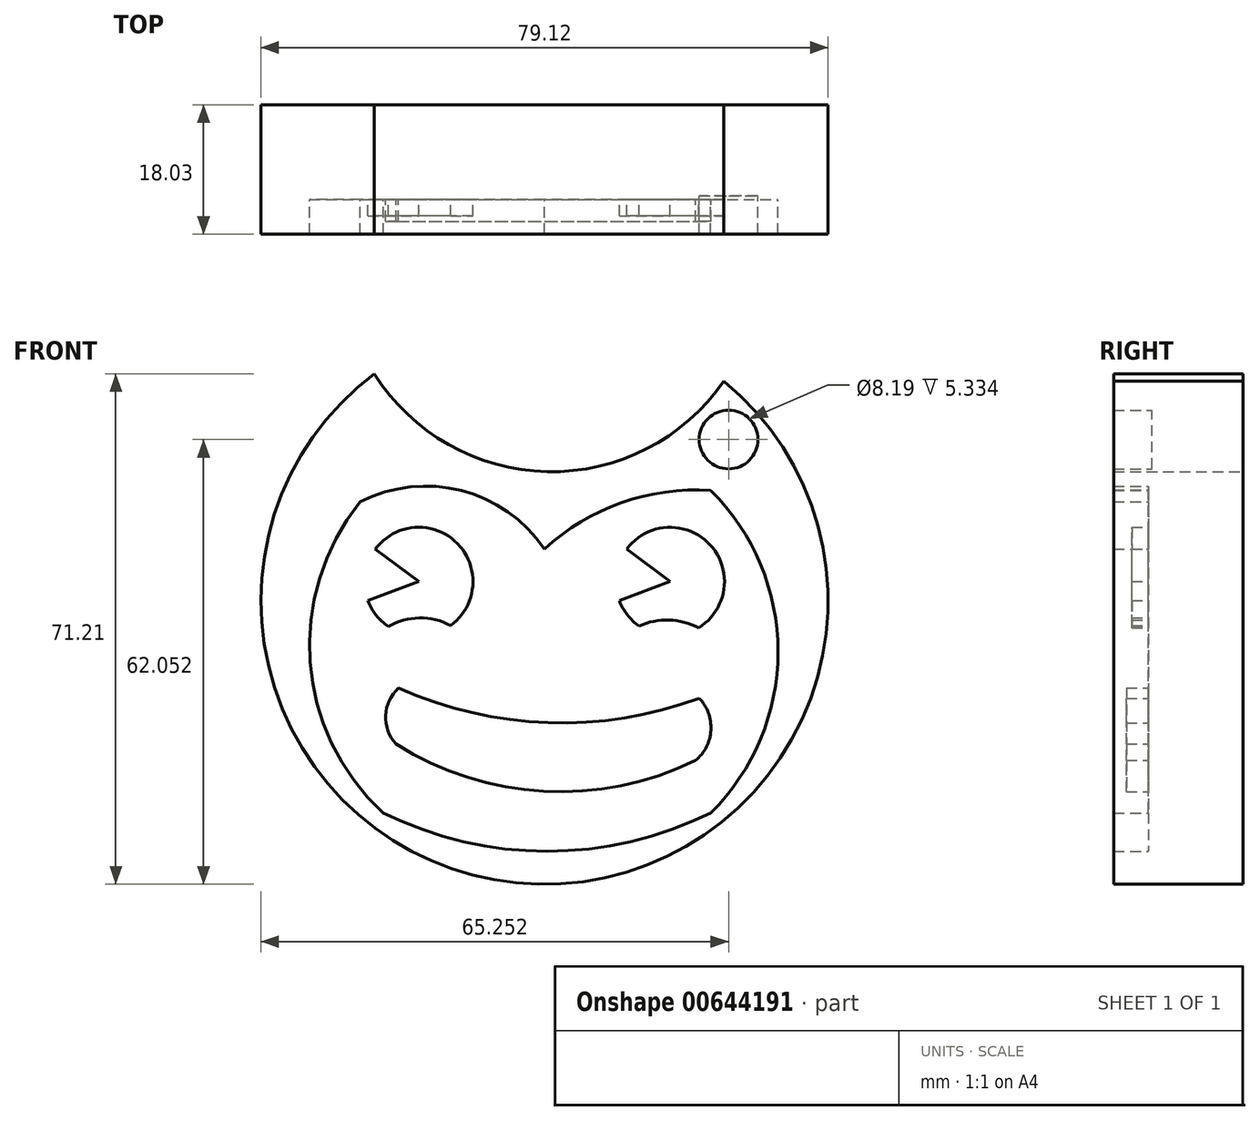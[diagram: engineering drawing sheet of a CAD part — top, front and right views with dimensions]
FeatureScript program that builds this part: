
annotation { "Feature Type Name" : "Feature", "Feature Type Description" : "" }
export const myFeature = defineFeature(function(context is Context, id is Id, definition is map)
    precondition{}
    {
        {
            var Q0;
            Q0=qCreatedBy(makeId("Front.planeOp"),FACE);
            var sketch = newSketch(context, id + "F0", { "sketchPlane" : qUnion([Q0])});
            skArc(sketch, "E0", {"start": v(-23.73, 31.65) * mm, "mid": v(-0.83, -39.55) * mm, "end": v(25.03, 30.64) * mm});
            skArc(sketch, "E1", {"start": v(-23.73, 31.65) * mm, "mid": v(0.38, 18) * mm, "end": v(25.03, 30.64) * mm});
            skSolve(sketch);
        }
        {
            var Q0;
            Q0=makeQuery(id+"F0.imprint","IMPRINT",FACE,{"disambiguationData":[TD([[makeQuery(id+"F0.imprint","IMPRINT",EDGE,{"derivedFrom":sQuery(id+"F0.wireOp",EDGE,"E0")}),1.0]])]});
            extrude(context, id + "F1", {"entities" : qUnion([Q0]), "depth" : 12.7 * mm, "offsetDistance" : 25.4 * mm});
        }
        {
            var Q0;
            Q0=makeQuery(id+"F1.opExtrude","CAP_FACE",FACE,{"disambiguationData":[OSD([sQuery(id+"F0.wireOp",EDGE,"E0"),sQuery(id+"F0.wireOp",EDGE,"E1")])],"isStart":false});
            var sketch = newSketch(context, id + "F2", { "sketchPlane" : qUnion([Q0])});
            skArc(sketch, "E2", {"start": v(-24.63, 0) * mm, "mid": v(-23.49, -2.01) * mm, "end": v(-21.8, -3.59) * mm});
            skArc(sketch, "E3.MirrorC", {"start": v(11.48, 7.2) * mm, "mid": v(23.13, 7.78) * mm, "end": v(21.5, -3.78) * mm});
            skLineSegment(sketch, "E4", {"start": v(-24.63, 0) * mm, "end": v(-17.54, 2.68) * mm});
            skLineSegment(sketch, "E5", {"start": v(-17.54, 2.68) * mm, "end": v(-23.61, 7.2) * mm});
            skLineSegment(sketch, "E6", {"start": v(10.46, 0) * mm, "end": v(17.54, 2.68) * mm});
            skLineSegment(sketch, "E7", {"start": v(17.54, 2.68) * mm, "end": v(11.48, 7.2) * mm});
            skArc(sketch, "E8", {"start": v(-10.05, -6.13) * mm, "mid": v(-17.34, -2.4) * mm, "end": v(-24.63, -6.13) * mm});
            skArc(sketch, "E9", {"start": v(25.16, -7.2) * mm, "mid": v(17.2, -2.69) * mm, "end": v(9.16, -7.02) * mm});
            skArc(sketch, "E10.trimOffspring", {"start": v(-13.1, -3.46) * mm, "mid": v(-12.15, 8) * mm, "end": v(-23.61, 7.2) * mm});
            skArc(sketch, "E11.trimOffspring", {"start": v(13.2, -3.53) * mm, "mid": v(11.57, -1.97) * mm, "end": v(10.46, 0) * mm});
            skSolve(sketch);
        }
        {
            var Q0;
            Q0=makeQuery(id+"F2.imprint","IMPRINT",FACE,{"disambiguationData":[TD([[makeQuery(id+"F2.imprint","IMPRINT",EDGE,{"derivedFrom":sQuery(id+"F2.wireOp",EDGE,"E2")}),-1.0]])]});
            var sketch = newSketch(context, id + "F3", { "sketchPlane" : qUnion([Q0])});
            skArc(sketch, "E12", {"start": v(-20.36, -12.18) * mm, "mid": v(0.48, -17.02) * mm, "end": v(21.6, -13.6) * mm});
            skArc(sketch, "E13", {"start": v(-20.71, -20) * mm, "mid": v(-0.11, -26.59) * mm, "end": v(21.09, -22.28) * mm});
            skArc(sketch, "E14", {"start": v(-20.36, -12.18) * mm, "mid": v(-22.16, -16.02) * mm, "end": v(-20.71, -20) * mm});
            skArc(sketch, "E15", {"start": v(21.09, -22.28) * mm, "mid": v(23.22, -18.05) * mm, "end": v(21.6, -13.6) * mm});
            skLineSegment(sketch, "E16", {"start": v(-17.1, -22.05) * mm, "end": v(-16.62, -13.7) * mm});
            skLineSegment(sketch, "E17", {"start": v(-12.7, -23.97) * mm, "end": v(-12.7, -14.97) * mm});
            skLineSegment(sketch, "E18", {"start": v(-8.35, -25.33) * mm, "end": v(-8.35, -16.27) * mm});
            skLineSegment(sketch, "E19", {"start": v(0, -26.6) * mm, "end": v(0, -17) * mm});
            skLineSegment(sketch, "E20", {"start": v(5.9, -26.5) * mm, "end": v(5.9, -16.94) * mm});
            skLineSegment(sketch, "E21", {"start": v(13.99, -25) * mm, "end": v(13.99, -16.27) * mm});
            skLineSegment(sketch, "E22", {"start": v(19.16, -23.17) * mm, "end": v(19.16, -14.44) * mm});
            skSolve(sketch);
        }
        {
            var Q0;
            Q0 = qSketchRegion(id + "F2", true);
            extrude(context, id + "F4", {"entities" : qUnion([Q0]), "operationType" : NewBodyOperationType.ADD, "depth" : 2.8 * mm, "offsetDistance" : 25.4 * mm});
        }
        {
            var Q0;
            Q0 = qSketchRegion(id + "F3", true);
            extrude(context, id + "F5", {"entities" : qUnion([Q0]), "operationType" : NewBodyOperationType.ADD, "depth" : 3.56 * mm, "offsetDistance" : 25.4 * mm});
        }
        {
            var Q0;
            Q0=makeQuery(id+"F1.opExtrude","CAP_FACE",FACE,{"disambiguationData":[OSD([sQuery(id+"F0.wireOp",EDGE,"E0"),sQuery(id+"F0.wireOp",EDGE,"E1")])],"isStart":false});
            var sketch = newSketch(context, id + "F6", { "sketchPlane" : qUnion([Q0])});
            skArc(sketch, "E23", {"start": v(-25.7, 13.78) * mm, "mid": v(-32.69, -8.55) * mm, "end": v(-22.5, -29.6) * mm});
            skArc(sketch, "E24", {"start": v(0, 7.2) * mm, "mid": v(-11.6, 15.37) * mm, "end": v(-25.7, 13.78) * mm});
            skArc(sketch, "E25", {"start": v(23.2, 15.37) * mm, "mid": v(10.75, 13.7) * mm, "end": v(0, 7.2) * mm});
            skPoint(sketch, "E25.startSnap0", {"position": v(-11.6, 15.37) * mm});
            skArc(sketch, "E26", {"start": v(23.2, -29.6) * mm, "mid": v(32.59, -7.12) * mm, "end": v(23.2, 15.37) * mm});
            skArc(sketch, "E27", {"start": v(-22.5, -29.6) * mm, "mid": v(0.36, -34.95) * mm, "end": v(23.2, -29.6) * mm});
            skSolve(sketch);
        }
        {
            var Q0;
            Q0 = qSketchRegion(id + "F6", true);
            extrude(context, id + "F7", {"entities" : qUnion([Q0]), "operationType" : NewBodyOperationType.ADD, "depth" : 0.5 * mm, "offsetDistance" : 25.4 * mm});
        }
        {
            var Q0;
            Q0=makeQuery(id+"F1.opExtrude","CAP_FACE",FACE,{"disambiguationData":[OSD([sQuery(id+"F0.wireOp",EDGE,"E0"),sQuery(id+"F0.wireOp",EDGE,"E1")])],"isStart":false});
            var sketch = newSketch(context, id + "F8", { "sketchPlane" : qUnion([Q0])});
            skCircle(sketch, "E28", {"center": v(25.7, 22.5) * mm, "radius": 4.1 * mm});
            skSolve(sketch);
        }
        {
            var Q0;
            Q0=makeQuery(id+"F8.imprint","IMPRINT",FACE,{"disambiguationData":[TD([[makeQuery(id+"F8.imprint","IMPRINT",EDGE,{"derivedFrom":sQuery(id+"F8.wireOp",EDGE,"E28")}),-1.0]])]});
            extrude(context, id + "F9", {"entities" : qUnion([Q0]), "operationType" : NewBodyOperationType.ADD, "depth" : 5.33 * mm, "offsetDistance" : 25.4 * mm});
        }
    });
